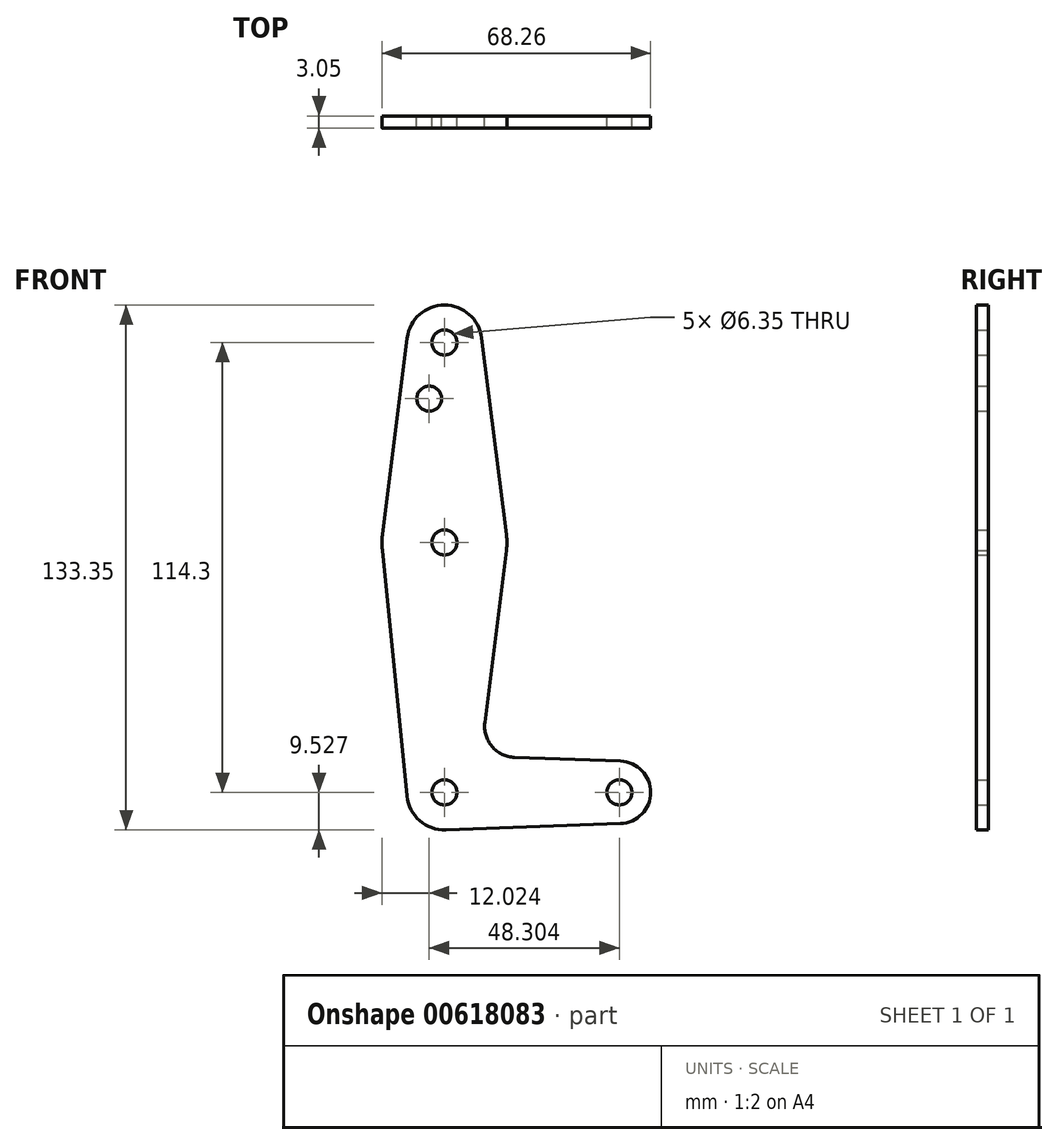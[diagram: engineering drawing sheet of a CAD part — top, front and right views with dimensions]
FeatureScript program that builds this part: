
annotation { "Feature Type Name" : "Feature", "Feature Type Description" : "" }
export const myFeature = defineFeature(function(context is Context, id is Id, definition is map)
    precondition{}
    {
        {
            var Q0;
            Q0=qCreatedBy(makeId("Front.planeOp"),FACE);
            var sketch = newSketch(context, id + "F0", { "sketchPlane" : qUnion([Q0])});
            skLineSegment(sketch, "E0", {"start": v(-37.01, 57.26) * mm, "end": v(-37.01, -57.04) * mm, "construction": true});
            skLineSegment(sketch, "E1", {"start": v(-37.01, -57.04) * mm, "end": v(7.44, -57.04) * mm, "construction": true});
            skCircle(sketch, "E2", {"center": v(-37.01, 57.26) * mm, "radius": 9.52 * mm});
            skCircle(sketch, "E3", {"center": v(-37.01, 6.46) * mm, "radius": 15.88 * mm});
            skCircle(sketch, "E4", {"center": v(-37.01, -57.04) * mm, "radius": 9.53 * mm});
            skCircle(sketch, "E5", {"center": v(7.44, -57.04) * mm, "radius": 7.94 * mm});
            skLineSegment(sketch, "E6", {"start": v(-46.46, 58.45) * mm, "end": v(-52.76, 8.44) * mm});
            skLineSegment(sketch, "E7", {"start": v(-52.76, 4.47) * mm, "end": v(-46.49, -58) * mm});
            skLineSegment(sketch, "E8", {"start": v(-26.77, -39.21) * mm, "end": v(-21.26, 4.47) * mm});
            skLineSegment(sketch, "E9", {"start": v(-19.16, -48.15) * mm, "end": v(7.72, -49.11) * mm});
            skLineSegment(sketch, "E10", {"start": v(7.72, -64.98) * mm, "end": v(-37.01, -66.57) * mm});
            skPoint(sketch, "E11.start.orphan", {"position": v(-21.26, 8.44) * mm});
            skLineSegment(sketch, "E12", {"start": v(-21.26, 8.44) * mm, "end": v(-27.58, 58.56) * mm});
            skCircle(sketch, "E13", {"center": v(-37.01, 57.26) * mm, "radius": 3.18 * mm});
            skCircle(sketch, "E14", {"center": v(-37.01, 6.46) * mm, "radius": 3.18 * mm});
            skCircle(sketch, "E15", {"center": v(-37.01, -57.04) * mm, "radius": 3.18 * mm});
            skCircle(sketch, "E16", {"center": v(7.44, -57.04) * mm, "radius": 3.18 * mm});
            skCircle(sketch, "E17", {"center": v(-40.87, 42.98) * mm, "radius": 3.18 * mm});
            skPoint(sketch, "E18.newPointA", {"position": v(-29.13, -58) * mm});
            skArc(sketch, "E18.filletArc", {"start": v(-26.77, -39.21) * mm, "mid": v(-24.93, -45.36) * mm, "end": v(-19.16, -48.15) * mm});
            skSolve(sketch);
        }
        {
            var Q0;
            {var subQ5=sQuery(id+"F0.wireOp",EDGE,"E6");Q0=makeQuery(id+"F0.imprint","IMPRINT",FACE,{"disambiguationData":[TD([[makeQuery(id+"F0.imprint","IMPRINT",EDGE,{"derivedFrom":subQ5}),1.0]])]});}
            var Q1;
            Q1=makeQuery(id+"F0.imprint","IMPRINT",FACE,{"disambiguationData":[TD([[makeQuery(id+"F0.imprint","IMPRINT",EDGE,{"derivedFrom":sQuery(id+"F0.wireOp",EDGE,"E14")}),-1.0]])]});
            var Q2;
            Q2=makeQuery(id+"F0.imprint","IMPRINT",FACE,{"disambiguationData":[TD([[makeQuery(id+"F0.imprint","IMPRINT",EDGE,{"derivedFrom":sQuery(id+"F0.wireOp",EDGE,"E13")}),-1.0]])]});
            var Q3;
            {var subQ0=sQuery(id+"F0.wireOp",EDGE,"E7");Q3=makeQuery(id+"F0.imprint","IMPRINT",FACE,{"disambiguationData":[TD([[makeQuery(id+"F0.imprint","IMPRINT",EDGE,{"derivedFrom":subQ0}),1.0]])]});}
            var Q4;
            Q4=makeQuery(id+"F0.imprint","IMPRINT",FACE,{"disambiguationData":[TD([[makeQuery(id+"F0.imprint","IMPRINT",EDGE,{"derivedFrom":sQuery(id+"F0.wireOp",EDGE,"E15")}),-1.0]])]});
            var Q5;
            Q5=makeQuery(id+"F0.imprint","IMPRINT",FACE,{"disambiguationData":[TD([[makeQuery(id+"F0.imprint","IMPRINT",EDGE,{"derivedFrom":sQuery(id+"F0.wireOp",EDGE,"E16")}),-1.0]])]});
            extrude(context, id + "F1", {"entities" : qUnion([Q0, Q1, Q2, Q3, Q4, Q5]), "depth" : 3.05 * mm, "offsetDistance" : 25.4 * mm});
        }
    });
